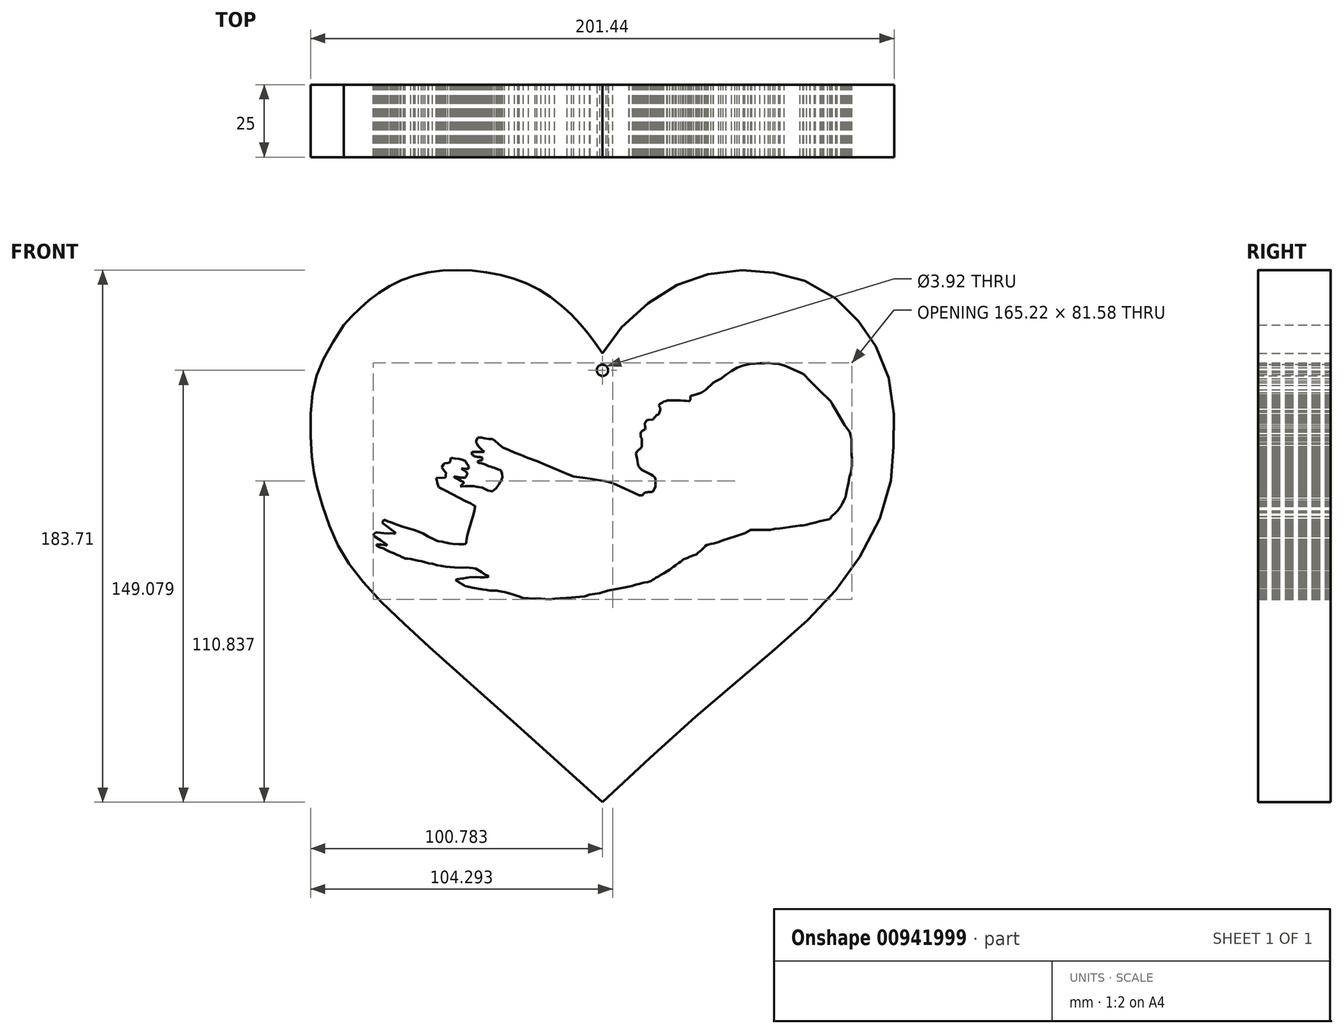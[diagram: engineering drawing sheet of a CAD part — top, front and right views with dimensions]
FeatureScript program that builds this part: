
annotation { "Feature Type Name" : "Feature", "Feature Type Description" : "" }
export const myFeature = defineFeature(function(context is Context, id is Id, definition is map)
    precondition{}
    {
        {
            var Q0;
            Q0=qCreatedBy(makeId("Front.planeOp"),FACE);
            var sketch = newSketch(context, id + "F0", { "sketchPlane" : qUnion([Q0])});
            skFitSpline(sketch, "E0", {"points": [v(-91.87, 46.62) * mm, v(-81.76, 56.16) * mm, v(-66.44, 63.96) * mm, v(-45.34, 65.12) * mm, v(-26.55, 59.92) * mm, v(-12.1, 48.93) * mm, v(-2.52, 36.86) * mm], "startDerivative": vector(63.3, 66.27) * mm, "endDerivative": vector(56.32, -78.36) * mm});
            skFitSpline(sketch, "E1", {"points": [v(-2.52, 36.86) * mm, v(5.39, 47.35) * mm, v(17.93, 57.31) * mm, v(29.62, 62.99) * mm, v(43.71, 65.4) * mm, v(56.26, 64.7) * mm, v(68.97, 61.1) * mm, v(81.7, 52.5) * mm, v(88.9, 43.74) * mm, v(95.1, 32.22) * mm, v(98.02, 16.24) * mm, v(97.85, 3) * mm, v(95.96, -12.11) * mm, v(86.85, -32.57) * mm, v(74.47, -49.06) * mm, v(57.8, -64.7) * mm, v(33.23, -85.5) * mm, v(-2.52, -118.15) * mm], "startDerivative": vector(138.08, 210.1) * mm, "endDerivative": vector(-379.46, -353.8) * mm});
            skFitSpline(sketch, "E2", {"points": [v(-2.52, -118.15) * mm, v(-50.8, -74.84) * mm, v(-83.63, -43.9) * mm, v(-95.32, -26.38) * mm, v(-100.82, -10.05) * mm, v(-102.7, 0) * mm, v(-103.05, 18.82) * mm, v(-99.79, 32.74) * mm, v(-91.87, 46.62) * mm], "startDerivative": vector(-238.07, 214.29) * mm, "endDerivative": vector(86.52, 135.51) * mm});
            skSolve(sketch);
        }
        {
            var Q0;
            Q0 = qSketchRegion(id + "F0", true);
            extrude(context, id + "F1", {"entities" : qUnion([Q0]), "depth" : 25 * mm, "offsetDistance" : 25 * mm});
        }
        {
            var Q0;
            Q0=qCreatedBy(makeId("Front.planeOp"),FACE);
            var sketch = newSketch(context, id + "F2", { "sketchPlane" : qUnion([Q0])});
            skLineSegment(sketch, "E3", {"start": v(-47.5, 2.74) * mm, "end": v(-43.27, 2.74) * mm});
            skLineSegment(sketch, "E4", {"start": v(-43.27, 2.74) * mm, "end": v(-44.61, 3.9) * mm});
            skLineSegment(sketch, "E5", {"start": v(-44.61, 3.9) * mm, "end": v(-45.36, 4.67) * mm});
            skLineSegment(sketch, "E6", {"start": v(-45.36, 4.67) * mm, "end": v(-45.88, 5.5) * mm});
            skLineSegment(sketch, "E7", {"start": v(-45.88, 5.5) * mm, "end": v(-46.11, 6) * mm});
            skLineSegment(sketch, "E8", {"start": v(-46.11, 6) * mm, "end": v(-46.11, 6.37) * mm});
            skLineSegment(sketch, "E9", {"start": v(-46.11, 6.37) * mm, "end": v(-46.11, 6.55) * mm});
            skLineSegment(sketch, "E10", {"start": v(-46.11, 6.55) * mm, "end": v(-45.84, 7.16) * mm});
            skLineSegment(sketch, "E11", {"start": v(-45.84, 7.16) * mm, "end": v(-45.54, 7.7) * mm});
            skLineSegment(sketch, "E12", {"start": v(-45.54, 7.7) * mm, "end": v(-45.2, 7.7) * mm});
            skLineSegment(sketch, "E13", {"start": v(-45.2, 7.7) * mm, "end": v(-44.32, 7.7) * mm});
            skLineSegment(sketch, "E14", {"start": v(-44.32, 7.7) * mm, "end": v(-43.25, 7.5) * mm});
            skLineSegment(sketch, "E15", {"start": v(-43.25, 7.5) * mm, "end": v(-41.85, 7.28) * mm});
            skLineSegment(sketch, "E16", {"start": v(-41.85, 7.28) * mm, "end": v(-40.8, 7.28) * mm});
            skLineSegment(sketch, "E17", {"start": v(-40.8, 7.28) * mm, "end": v(-40.46, 7.28) * mm});
            skLineSegment(sketch, "E18", {"start": v(-40.46, 7.28) * mm, "end": v(-39.65, 6.55) * mm});
            skLineSegment(sketch, "E19", {"start": v(-39.65, 6.55) * mm, "end": v(-38.36, 5.41) * mm});
            skLineSegment(sketch, "E20", {"start": v(-38.36, 5.41) * mm, "end": v(-37.02, 4.35) * mm});
            skLineSegment(sketch, "E21", {"start": v(-37.02, 4.35) * mm, "end": v(-34.84, 3.4) * mm});
            skLineSegment(sketch, "E22", {"start": v(-34.84, 3.4) * mm, "end": v(-32.85, 2.55) * mm});
            skLineSegment(sketch, "E23", {"start": v(-32.85, 2.55) * mm, "end": v(-30.76, 1.72) * mm});
            skLineSegment(sketch, "E24", {"start": v(-30.76, 1.72) * mm, "end": v(-28.4, 0.79) * mm});
            skLineSegment(sketch, "E25", {"start": v(-28.4, 0.79) * mm, "end": v(-25.18, -0.46) * mm});
            skLineSegment(sketch, "E26", {"start": v(-25.18, -0.46) * mm, "end": v(-22.25, -1.73) * mm});
            skLineSegment(sketch, "E27", {"start": v(-22.25, -1.73) * mm, "end": v(-18.33, -3.37) * mm});
            skLineSegment(sketch, "E28", {"start": v(-18.33, -3.37) * mm, "end": v(-14.77, -4.82) * mm});
            skLineSegment(sketch, "E29", {"start": v(-14.77, -4.82) * mm, "end": v(-12.5, -5.8) * mm});
            skLineSegment(sketch, "E30", {"start": v(-12.5, -5.8) * mm, "end": v(-9.4, -6.15) * mm});
            skLineSegment(sketch, "E31", {"start": v(-9.4, -6.15) * mm, "end": v(-6.74, -6.47) * mm});
            skLineSegment(sketch, "E32", {"start": v(-6.74, -6.47) * mm, "end": v(-3.68, -7.02) * mm});
            skLineSegment(sketch, "E33", {"start": v(-3.68, -7.02) * mm, "end": v(-1.27, -7.45) * mm});
            skLineSegment(sketch, "E34", {"start": v(-1.27, -7.45) * mm, "end": v(0.97, -8.08) * mm});
            skLineSegment(sketch, "E35", {"start": v(0.97, -8.08) * mm, "end": v(2.95, -8.93) * mm});
            skLineSegment(sketch, "E36", {"start": v(2.95, -8.93) * mm, "end": v(5.15, -9.88) * mm});
            skLineSegment(sketch, "E37", {"start": v(5.15, -9.88) * mm, "end": v(6.66, -10.53) * mm});
            skLineSegment(sketch, "E38", {"start": v(6.66, -10.53) * mm, "end": v(8.24, -11.37) * mm});
            skLineSegment(sketch, "E39", {"start": v(8.24, -11.37) * mm, "end": v(9.38, -11.86) * mm});
            skLineSegment(sketch, "E40", {"start": v(9.38, -11.86) * mm, "end": v(10.1, -12.17) * mm});
            skLineSegment(sketch, "E41", {"start": v(10.1, -12.17) * mm, "end": v(10.85, -12.17) * mm});
            skLineSegment(sketch, "E42", {"start": v(10.85, -12.17) * mm, "end": v(11.25, -12.17) * mm});
            skLineSegment(sketch, "E43", {"start": v(11.25, -12.17) * mm, "end": v(11.52, -11.84) * mm});
            skLineSegment(sketch, "E44", {"start": v(11.52, -11.84) * mm, "end": v(11.78, -11.63) * mm});
            skLineSegment(sketch, "E45", {"start": v(11.78, -11.63) * mm, "end": v(12.21, -11.25) * mm});
            skLineSegment(sketch, "E46", {"start": v(12.21, -11.25) * mm, "end": v(12.35, -11.25) * mm});
            skLineSegment(sketch, "E47", {"start": v(12.35, -11.25) * mm, "end": v(12.8, -11.19) * mm});
            skLineSegment(sketch, "E48", {"start": v(12.8, -11.19) * mm, "end": v(13.3, -11.12) * mm});
            skLineSegment(sketch, "E49", {"start": v(13.3, -11.12) * mm, "end": v(13.95, -11.12) * mm});
            skLineSegment(sketch, "E50", {"start": v(13.95, -11.12) * mm, "end": v(14.61, -11.08) * mm});
            skLineSegment(sketch, "E51", {"start": v(14.61, -11.08) * mm, "end": v(15, -10.85) * mm});
            skLineSegment(sketch, "E52", {"start": v(15, -10.85) * mm, "end": v(15.18, -10.41) * mm});
            skLineSegment(sketch, "E53", {"start": v(15.18, -10.41) * mm, "end": v(15.4, -9.88) * mm});
            skLineSegment(sketch, "E54", {"start": v(15.4, -9.88) * mm, "end": v(15.7, -9.2) * mm});
            skLineSegment(sketch, "E55", {"start": v(15.7, -9.2) * mm, "end": v(15.7, -7.4) * mm});
            skLineSegment(sketch, "E56", {"start": v(15.7, -7.4) * mm, "end": v(15.7, -6.76) * mm});
            skLineSegment(sketch, "E57", {"start": v(15.7, -6.76) * mm, "end": v(15.6, -6.08) * mm});
            skLineSegment(sketch, "E58", {"start": v(15.6, -6.08) * mm, "end": v(14.76, -5.4) * mm});
            skLineSegment(sketch, "E59", {"start": v(14.76, -5.4) * mm, "end": v(14.08, -4.98) * mm});
            skLineSegment(sketch, "E60", {"start": v(14.08, -4.98) * mm, "end": v(11.04, -3.46) * mm});
            skLineSegment(sketch, "E61", {"start": v(11.04, -3.46) * mm, "end": v(10.3, -2.72) * mm});
            skLineSegment(sketch, "E62", {"start": v(10.3, -2.72) * mm, "end": v(9.79, -1.95) * mm});
            skLineSegment(sketch, "E63", {"start": v(9.79, -1.95) * mm, "end": v(9.58, -0.4) * mm});
            skLineSegment(sketch, "E64", {"start": v(9.58, -0.4) * mm, "end": v(9.44, 0.6) * mm});
            skLineSegment(sketch, "E65", {"start": v(9.44, 0.6) * mm, "end": v(9.16, 1.53) * mm});
            skLineSegment(sketch, "E66", {"start": v(9.16, 1.53) * mm, "end": v(9.07, 2.19) * mm});
            skLineSegment(sketch, "E67", {"start": v(9.07, 2.19) * mm, "end": v(9.3, 2.72) * mm});
            skLineSegment(sketch, "E68", {"start": v(9.3, 2.72) * mm, "end": v(9.79, 3.34) * mm});
            skLineSegment(sketch, "E69", {"start": v(9.79, 3.34) * mm, "end": v(10.83, 4.16) * mm});
            skLineSegment(sketch, "E70", {"start": v(10.83, 4.16) * mm, "end": v(11.06, 4.7) * mm});
            skLineSegment(sketch, "E71", {"start": v(11.06, 4.7) * mm, "end": v(11.06, 7.11) * mm});
            skLineSegment(sketch, "E72", {"start": v(11.06, 7.11) * mm, "end": v(11.02, 7.43) * mm});
            skLineSegment(sketch, "E73", {"start": v(11.02, 7.43) * mm, "end": v(10.67, 7.85) * mm});
            skLineSegment(sketch, "E74", {"start": v(10.67, 7.85) * mm, "end": v(10.63, 8.54) * mm});
            skLineSegment(sketch, "E75", {"start": v(10.63, 8.54) * mm, "end": v(10.53, 8.8) * mm});
            skLineSegment(sketch, "E76", {"start": v(10.53, 8.8) * mm, "end": v(10.77, 9.68) * mm});
            skLineSegment(sketch, "E77", {"start": v(10.77, 9.68) * mm, "end": v(11.35, 10.08) * mm});
            skLineSegment(sketch, "E78", {"start": v(11.35, 10.08) * mm, "end": v(11.63, 10.21) * mm});
            skLineSegment(sketch, "E79", {"start": v(11.63, 10.21) * mm, "end": v(11.87, 10.37) * mm});
            skLineSegment(sketch, "E80", {"start": v(11.87, 10.37) * mm, "end": v(12.21, 10.55) * mm});
            skLineSegment(sketch, "E81", {"start": v(12.21, 10.55) * mm, "end": v(12.3, 10.74) * mm});
            skLineSegment(sketch, "E82", {"start": v(12.3, 10.74) * mm, "end": v(12.25, 11.45) * mm});
            skPoint(sketch, "E82.endSnap0", {"position": v(12.25, 10.65) * mm});
            skLineSegment(sketch, "E83", {"start": v(12.25, 11.45) * mm, "end": v(12.13, 12.34) * mm});
            skLineSegment(sketch, "E84", {"start": v(12.13, 12.34) * mm, "end": v(12.1, 12.64) * mm});
            skLineSegment(sketch, "E85", {"start": v(12.1, 12.64) * mm, "end": v(12.3, 12.97) * mm});
            skLineSegment(sketch, "E86", {"start": v(12.3, 12.97) * mm, "end": v(12.54, 13.41) * mm});
            skLineSegment(sketch, "E87", {"start": v(12.54, 13.41) * mm, "end": v(12.73, 13.73) * mm});
            skLineSegment(sketch, "E88", {"start": v(12.73, 13.73) * mm, "end": v(13.3, 13.8) * mm});
            skLineSegment(sketch, "E89", {"start": v(13.3, 13.8) * mm, "end": v(14.96, 13.96) * mm});
            skLineSegment(sketch, "E90", {"start": v(14.96, 13.96) * mm, "end": v(15.3, 14.43) * mm});
            skLineSegment(sketch, "E91", {"start": v(15.3, 14.43) * mm, "end": v(15.76, 15.03) * mm});
            skLineSegment(sketch, "E92", {"start": v(15.76, 15.03) * mm, "end": v(16.15, 15.46) * mm});
            skLineSegment(sketch, "E93", {"start": v(16.15, 15.46) * mm, "end": v(16.55, 15.66) * mm});
            skLineSegment(sketch, "E94", {"start": v(16.55, 15.66) * mm, "end": v(16.88, 15.7) * mm});
            skLineSegment(sketch, "E95", {"start": v(16.88, 15.7) * mm, "end": v(17.2, 16.44) * mm});
            skLineSegment(sketch, "E96", {"start": v(17.2, 16.44) * mm, "end": v(17.4, 17.14) * mm});
            skLineSegment(sketch, "E97", {"start": v(17.4, 17.14) * mm, "end": v(17.4, 17.7) * mm});
            skLineSegment(sketch, "E98", {"start": v(17.4, 17.7) * mm, "end": v(17.4, 17.97) * mm});
            skLineSegment(sketch, "E99", {"start": v(17.4, 17.97) * mm, "end": v(17.19, 18.4) * mm});
            skLineSegment(sketch, "E100", {"start": v(17.19, 18.4) * mm, "end": v(16.94, 18.75) * mm});
            skLineSegment(sketch, "E101", {"start": v(16.94, 18.75) * mm, "end": v(17.02, 19) * mm});
            skLineSegment(sketch, "E102", {"start": v(17.02, 19) * mm, "end": v(17.4, 19.35) * mm});
            skLineSegment(sketch, "E103", {"start": v(17.4, 19.35) * mm, "end": v(18.2, 19.82) * mm});
            skLineSegment(sketch, "E104", {"start": v(18.2, 19.82) * mm, "end": v(18.59, 20.18) * mm});
            skLineSegment(sketch, "E105", {"start": v(18.59, 20.18) * mm, "end": v(19.28, 20.35) * mm});
            skLineSegment(sketch, "E106", {"start": v(19.28, 20.35) * mm, "end": v(19.94, 20.51) * mm});
            skLineSegment(sketch, "E107", {"start": v(19.94, 20.51) * mm, "end": v(21.56, 20.6) * mm});
            skLineSegment(sketch, "E108", {"start": v(21.56, 20.6) * mm, "end": v(22.93, 20.6) * mm});
            skLineSegment(sketch, "E109", {"start": v(22.93, 20.6) * mm, "end": v(24.37, 20.6) * mm});
            skLineSegment(sketch, "E110", {"start": v(24.37, 20.6) * mm, "end": v(25.5, 20.49) * mm});
            skLineSegment(sketch, "E111", {"start": v(25.5, 20.49) * mm, "end": v(26.3, 20.4) * mm});
            skLineSegment(sketch, "E112", {"start": v(26.3, 20.4) * mm, "end": v(27.3, 20.33) * mm});
            skLineSegment(sketch, "E113", {"start": v(27.3, 20.33) * mm, "end": v(27.61, 20.37) * mm});
            skLineSegment(sketch, "E114", {"start": v(27.61, 20.37) * mm, "end": v(27.75, 20.83) * mm});
            skLineSegment(sketch, "E115", {"start": v(27.75, 20.83) * mm, "end": v(27.86, 21.46) * mm});
            skLineSegment(sketch, "E116", {"start": v(27.86, 21.46) * mm, "end": v(27.86, 21.9) * mm});
            skLineSegment(sketch, "E117", {"start": v(27.86, 21.9) * mm, "end": v(28.05, 22.17) * mm});
            skLineSegment(sketch, "E118", {"start": v(28.05, 22.17) * mm, "end": v(28.38, 22.22) * mm});
            skLineSegment(sketch, "E119", {"start": v(28.38, 22.22) * mm, "end": v(29.73, 22.55) * mm});
            skLineSegment(sketch, "E120", {"start": v(29.73, 22.55) * mm, "end": v(31.6, 23.26) * mm});
            skLineSegment(sketch, "E121", {"start": v(31.6, 23.26) * mm, "end": v(33.1, 24.27) * mm});
            skLineSegment(sketch, "E122", {"start": v(33.1, 24.27) * mm, "end": v(34.17, 25.3) * mm});
            skLineSegment(sketch, "E123", {"start": v(34.17, 25.3) * mm, "end": v(34.87, 25.96) * mm});
            skLineSegment(sketch, "E124", {"start": v(34.87, 25.96) * mm, "end": v(35.62, 26.67) * mm});
            skLineSegment(sketch, "E125", {"start": v(35.62, 26.67) * mm, "end": v(36.62, 27.17) * mm});
            skLineSegment(sketch, "E126", {"start": v(36.62, 27.17) * mm, "end": v(38.33, 28) * mm});
            skLineSegment(sketch, "E127", {"start": v(38.33, 28) * mm, "end": v(40.14, 29.43) * mm});
            skLineSegment(sketch, "E128", {"start": v(40.14, 29.43) * mm, "end": v(42.03, 30.7) * mm});
            skLineSegment(sketch, "E129", {"start": v(42.03, 30.7) * mm, "end": v(43.95, 31.81) * mm});
            skLineSegment(sketch, "E130", {"start": v(43.95, 31.81) * mm, "end": v(46.1, 32.63) * mm});
            skLineSegment(sketch, "E131", {"start": v(46.1, 32.63) * mm, "end": v(47.79, 33.04) * mm});
            skLineSegment(sketch, "E132", {"start": v(47.79, 33.04) * mm, "end": v(48.97, 33.2) * mm});
            skLineSegment(sketch, "E133", {"start": v(48.97, 33.2) * mm, "end": v(50.22, 33.32) * mm});
            skLineSegment(sketch, "E134", {"start": v(50.22, 33.32) * mm, "end": v(51.83, 33.4) * mm});
            skLineSegment(sketch, "E135", {"start": v(51.83, 33.4) * mm, "end": v(53.49, 33.4) * mm});
            skLineSegment(sketch, "E136", {"start": v(53.49, 33.4) * mm, "end": v(54.73, 33.48) * mm});
            skLineSegment(sketch, "E137", {"start": v(54.73, 33.48) * mm, "end": v(56.4, 33.32) * mm});
            skLineSegment(sketch, "E138", {"start": v(56.4, 33.32) * mm, "end": v(58.33, 33.1) * mm});
            skLineSegment(sketch, "E139", {"start": v(58.33, 33.1) * mm, "end": v(60.14, 32.56) * mm});
            skLineSegment(sketch, "E140", {"start": v(60.14, 32.56) * mm, "end": v(61.58, 31.94) * mm});
            skLineSegment(sketch, "E141", {"start": v(61.58, 31.94) * mm, "end": v(63.42, 31.15) * mm});
            skLineSegment(sketch, "E142", {"start": v(63.42, 31.15) * mm, "end": v(65.68, 30.18) * mm});
            skLineSegment(sketch, "E143", {"start": v(65.68, 30.18) * mm, "end": v(66.92, 29.5) * mm});
            skLineSegment(sketch, "E144", {"start": v(66.92, 29.5) * mm, "end": v(69.13, 27.34) * mm});
            skLineSegment(sketch, "E145", {"start": v(69.13, 27.34) * mm, "end": v(70.65, 25.73) * mm});
            skLineSegment(sketch, "E146", {"start": v(70.65, 25.73) * mm, "end": v(73.16, 23.23) * mm});
            skLineSegment(sketch, "E147", {"start": v(73.16, 23.23) * mm, "end": v(75.14, 21.34) * mm});
            skLineSegment(sketch, "E148", {"start": v(75.14, 21.34) * mm, "end": v(76.28, 20.14) * mm});
            skLineSegment(sketch, "E149", {"start": v(76.28, 20.14) * mm, "end": v(76.87, 19.2) * mm});
            skLineSegment(sketch, "E150", {"start": v(76.87, 19.2) * mm, "end": v(78.4, 16.66) * mm});
            skLineSegment(sketch, "E151", {"start": v(78.4, 16.66) * mm, "end": v(79.82, 14.22) * mm});
            skLineSegment(sketch, "E152", {"start": v(79.82, 14.22) * mm, "end": v(81, 12.1) * mm});
            skLineSegment(sketch, "E153", {"start": v(81, 12.1) * mm, "end": v(82.78, 9.6) * mm});
            skLineSegment(sketch, "E154", {"start": v(82.78, 9.6) * mm, "end": v(83.1, 8.73) * mm});
            skLineSegment(sketch, "E155", {"start": v(83.1, 8.73) * mm, "end": v(83.49, 7.11) * mm});
            skLineSegment(sketch, "E156", {"start": v(83.49, 7.11) * mm, "end": v(83.49, 4.84) * mm});
            skLineSegment(sketch, "E157", {"start": v(83.49, 4.84) * mm, "end": v(83.49, 2.17) * mm});
            skLineSegment(sketch, "E158", {"start": v(83.49, 2.17) * mm, "end": v(83.6, 0.2) * mm});
            skLineSegment(sketch, "E159", {"start": v(83.6, 0.2) * mm, "end": v(83.6, -1.95) * mm});
            skLineSegment(sketch, "E160", {"start": v(83.6, -1.95) * mm, "end": v(83.46, -2.93) * mm});
            skLineSegment(sketch, "E161", {"start": v(83.46, -2.93) * mm, "end": v(83.22, -4.44) * mm});
            skLineSegment(sketch, "E162", {"start": v(83.22, -4.44) * mm, "end": v(82.93, -5.4) * mm});
            skLineSegment(sketch, "E163", {"start": v(82.93, -5.4) * mm, "end": v(82.74, -6.05) * mm});
            skLineSegment(sketch, "E164", {"start": v(82.74, -6.05) * mm, "end": v(82.41, -7.75) * mm});
            skLineSegment(sketch, "E165", {"start": v(82.41, -7.75) * mm, "end": v(82.22, -8.93) * mm});
            skLineSegment(sketch, "E166", {"start": v(82.22, -8.93) * mm, "end": v(81.9, -9.98) * mm});
            skLineSegment(sketch, "E167", {"start": v(81.9, -9.98) * mm, "end": v(81.54, -11.88) * mm});
            skLineSegment(sketch, "E168", {"start": v(81.54, -11.88) * mm, "end": v(81.42, -12.68) * mm});
            skLineSegment(sketch, "E169", {"start": v(81.42, -12.68) * mm, "end": v(81.07, -13.49) * mm});
            skLineSegment(sketch, "E170", {"start": v(81.07, -13.49) * mm, "end": v(80.78, -14.07) * mm});
            skLineSegment(sketch, "E171", {"start": v(80.78, -14.07) * mm, "end": v(80.41, -14.7) * mm});
            skLineSegment(sketch, "E172", {"start": v(80.41, -14.7) * mm, "end": v(80.14, -15.21) * mm});
            skLineSegment(sketch, "E173", {"start": v(80.14, -15.21) * mm, "end": v(79.77, -16.08) * mm});
            skLineSegment(sketch, "E174", {"start": v(79.77, -16.08) * mm, "end": v(78.51, -17.63) * mm});
            skLineSegment(sketch, "E175", {"start": v(78.51, -17.63) * mm, "end": v(77.97, -18.14) * mm});
            skLineSegment(sketch, "E176", {"start": v(77.97, -18.14) * mm, "end": v(77.2, -18.92) * mm});
            skLineSegment(sketch, "E177", {"start": v(77.2, -18.92) * mm, "end": v(76.5, -19.62) * mm});
            skLineSegment(sketch, "E178", {"start": v(76.5, -19.62) * mm, "end": v(76.16, -20.13) * mm});
            skLineSegment(sketch, "E179", {"start": v(76.16, -20.13) * mm, "end": v(75.93, -20.46) * mm});
            skLineSegment(sketch, "E180", {"start": v(75.93, -20.46) * mm, "end": v(75.16, -20.64) * mm});
            skLineSegment(sketch, "E181", {"start": v(75.16, -20.64) * mm, "end": v(73.97, -20.8) * mm});
            skLineSegment(sketch, "E182", {"start": v(73.97, -20.8) * mm, "end": v(73.4, -21.02) * mm});
            skLineSegment(sketch, "E183", {"start": v(73.4, -21.02) * mm, "end": v(72.61, -21.12) * mm});
            skLineSegment(sketch, "E184", {"start": v(72.61, -21.12) * mm, "end": v(70.97, -21.6) * mm});
            skLineSegment(sketch, "E185", {"start": v(70.97, -21.6) * mm, "end": v(69.25, -21.96) * mm});
            skLineSegment(sketch, "E186", {"start": v(69.25, -21.96) * mm, "end": v(67.97, -22.33) * mm});
            skLineSegment(sketch, "E187", {"start": v(67.97, -22.33) * mm, "end": v(66.72, -22.58) * mm});
            skLineSegment(sketch, "E188", {"start": v(66.72, -22.58) * mm, "end": v(65.64, -22.65) * mm});
            skLineSegment(sketch, "E189", {"start": v(65.64, -22.65) * mm, "end": v(64.03, -22.86) * mm});
            skLineSegment(sketch, "E190", {"start": v(64.03, -22.86) * mm, "end": v(62.55, -23.07) * mm});
            skLineSegment(sketch, "E191", {"start": v(62.55, -23.07) * mm, "end": v(60.79, -23.3) * mm});
            skLineSegment(sketch, "E192", {"start": v(60.79, -23.3) * mm, "end": v(58.74, -23.58) * mm});
            skLineSegment(sketch, "E193", {"start": v(58.74, -23.58) * mm, "end": v(56.96, -23.74) * mm});
            skLineSegment(sketch, "E194", {"start": v(56.96, -23.74) * mm, "end": v(55.38, -24.2) * mm});
            skLineSegment(sketch, "E195", {"start": v(55.38, -24.2) * mm, "end": v(51.48, -24.2) * mm});
            skLineSegment(sketch, "E196", {"start": v(51.48, -24.2) * mm, "end": v(48.66, -24.2) * mm});
            skLineSegment(sketch, "E197", {"start": v(48.66, -24.2) * mm, "end": v(46.55, -25.27) * mm});
            skLineSegment(sketch, "E198", {"start": v(46.55, -25.27) * mm, "end": v(44.7, -25.97) * mm});
            skLineSegment(sketch, "E199", {"start": v(44.7, -25.97) * mm, "end": v(43.12, -26.44) * mm});
            skLineSegment(sketch, "E200", {"start": v(43.12, -26.44) * mm, "end": v(39.07, -27.73) * mm});
            skLineSegment(sketch, "E201", {"start": v(39.07, -27.73) * mm, "end": v(37.6, -28.28) * mm});
            skLineSegment(sketch, "E202", {"start": v(37.6, -28.28) * mm, "end": v(36.66, -28.56) * mm});
            skLineSegment(sketch, "E203", {"start": v(36.66, -28.56) * mm, "end": v(35.83, -28.8) * mm});
            skLineSegment(sketch, "E204", {"start": v(35.83, -28.8) * mm, "end": v(34.93, -28.99) * mm});
            skLineSegment(sketch, "E205", {"start": v(34.93, -28.99) * mm, "end": v(34.06, -29.24) * mm});
            skLineSegment(sketch, "E206", {"start": v(34.06, -29.24) * mm, "end": v(33.56, -29.38) * mm});
            skLineSegment(sketch, "E207", {"start": v(33.56, -29.38) * mm, "end": v(32.88, -29.78) * mm});
            skLineSegment(sketch, "E208", {"start": v(32.88, -29.78) * mm, "end": v(32.68, -30.15) * mm});
            skLineSegment(sketch, "E209", {"start": v(32.68, -30.15) * mm, "end": v(31.9, -30.94) * mm});
            skLineSegment(sketch, "E210", {"start": v(31.9, -30.94) * mm, "end": v(31.66, -31.1) * mm});
            skLineSegment(sketch, "E211", {"start": v(31.66, -31.1) * mm, "end": v(30.94, -31.65) * mm});
            skLineSegment(sketch, "E212", {"start": v(30.94, -31.65) * mm, "end": v(30.54, -32.05) * mm});
            skLineSegment(sketch, "E213", {"start": v(30.54, -32.05) * mm, "end": v(30.07, -32.46) * mm});
            skLineSegment(sketch, "E214", {"start": v(30.07, -32.46) * mm, "end": v(29.81, -32.68) * mm});
            skLineSegment(sketch, "E215", {"start": v(29.81, -32.68) * mm, "end": v(28.92, -32.97) * mm});
            skLineSegment(sketch, "E216", {"start": v(28.92, -32.97) * mm, "end": v(27.92, -33.35) * mm});
            skLineSegment(sketch, "E217", {"start": v(27.92, -33.35) * mm, "end": v(27.37, -33.57) * mm});
            skLineSegment(sketch, "E218", {"start": v(27.37, -33.57) * mm, "end": v(26.93, -33.82) * mm});
            skLineSegment(sketch, "E219", {"start": v(26.93, -33.82) * mm, "end": v(26.18, -34.04) * mm});
            skLineSegment(sketch, "E220", {"start": v(26.18, -34.04) * mm, "end": v(25.39, -34.34) * mm});
            skLineSegment(sketch, "E221", {"start": v(25.39, -34.34) * mm, "end": v(25, -34.65) * mm});
            skLineSegment(sketch, "E222", {"start": v(25, -34.65) * mm, "end": v(24.37, -35.2) * mm});
            skLineSegment(sketch, "E223", {"start": v(24.37, -35.2) * mm, "end": v(23.7, -35.6) * mm});
            skLineSegment(sketch, "E224", {"start": v(23.7, -35.6) * mm, "end": v(22.93, -36.14) * mm});
            skLineSegment(sketch, "E225", {"start": v(22.93, -36.14) * mm, "end": v(22.6, -36.45) * mm});
            skLineSegment(sketch, "E226", {"start": v(22.6, -36.45) * mm, "end": v(21.98, -36.91) * mm});
            skLineSegment(sketch, "E227", {"start": v(21.98, -36.91) * mm, "end": v(21.37, -37.39) * mm});
            skLineSegment(sketch, "E228", {"start": v(21.37, -37.39) * mm, "end": v(20.73, -37.9) * mm});
            skLineSegment(sketch, "E229", {"start": v(20.73, -37.9) * mm, "end": v(19.69, -38.53) * mm});
            skLineSegment(sketch, "E230", {"start": v(19.69, -38.53) * mm, "end": v(18.72, -39.1) * mm});
            skLineSegment(sketch, "E231", {"start": v(18.72, -39.1) * mm, "end": v(17.65, -39.7) * mm});
            skLineSegment(sketch, "E232", {"start": v(17.65, -39.7) * mm, "end": v(16.76, -40.26) * mm});
            skLineSegment(sketch, "E233", {"start": v(16.76, -40.26) * mm, "end": v(15.93, -40.72) * mm});
            skLineSegment(sketch, "E234", {"start": v(15.93, -40.72) * mm, "end": v(15.18, -41.13) * mm});
            skLineSegment(sketch, "E235", {"start": v(15.18, -41.13) * mm, "end": v(14.67, -41.46) * mm});
            skLineSegment(sketch, "E236", {"start": v(14.67, -41.46) * mm, "end": v(14.17, -41.76) * mm});
            skLineSegment(sketch, "E237", {"start": v(14.17, -41.76) * mm, "end": v(13.07, -42.18) * mm});
            skLineSegment(sketch, "E238", {"start": v(13.07, -42.18) * mm, "end": v(11.98, -42.37) * mm});
            skLineSegment(sketch, "E239", {"start": v(11.98, -42.37) * mm, "end": v(10.97, -42.57) * mm});
            skLineSegment(sketch, "E240", {"start": v(10.97, -42.57) * mm, "end": v(10.15, -42.77) * mm});
            skLineSegment(sketch, "E241", {"start": v(10.15, -42.77) * mm, "end": v(9.46, -42.98) * mm});
            skLineSegment(sketch, "E242", {"start": v(9.46, -42.98) * mm, "end": v(8.48, -43.2) * mm});
            skLineSegment(sketch, "E243", {"start": v(8.48, -43.2) * mm, "end": v(7.88, -43.43) * mm});
            skLineSegment(sketch, "E244", {"start": v(7.88, -43.43) * mm, "end": v(6.76, -43.67) * mm});
            skLineSegment(sketch, "E245", {"start": v(6.76, -43.67) * mm, "end": v(5.45, -43.91) * mm});
            skLineSegment(sketch, "E246", {"start": v(5.45, -43.91) * mm, "end": v(-0.58, -45.12) * mm});
            skLineSegment(sketch, "E247", {"start": v(-0.58, -45.12) * mm, "end": v(-3.49, -46) * mm});
            skLineSegment(sketch, "E248", {"start": v(-3.49, -46) * mm, "end": v(-6.97, -46.46) * mm});
            skLineSegment(sketch, "E249", {"start": v(-6.97, -46.46) * mm, "end": v(-8.83, -47.17) * mm});
            skLineSegment(sketch, "E250", {"start": v(-8.83, -47.17) * mm, "end": v(-10.42, -47.2) * mm});
            skLineSegment(sketch, "E251", {"start": v(-10.42, -47.2) * mm, "end": v(-13.16, -47.58) * mm});
            skLineSegment(sketch, "E252", {"start": v(-13.16, -47.58) * mm, "end": v(-16.48, -47.76) * mm});
            skLineSegment(sketch, "E253", {"start": v(-16.48, -47.76) * mm, "end": v(-19.08, -47.9) * mm});
            skLineSegment(sketch, "E254", {"start": v(-19.08, -47.9) * mm, "end": v(-20.77, -48.1) * mm});
            skLineSegment(sketch, "E255", {"start": v(-20.77, -48.1) * mm, "end": v(-23.75, -47.9) * mm});
            skLineSegment(sketch, "E256", {"start": v(-23.75, -47.9) * mm, "end": v(-25.76, -47.95) * mm});
            skLineSegment(sketch, "E257", {"start": v(-25.76, -47.95) * mm, "end": v(-28.12, -47.79) * mm});
            skLineSegment(sketch, "E258", {"start": v(-28.12, -47.79) * mm, "end": v(-29.88, -47.79) * mm});
            skLineSegment(sketch, "E259", {"start": v(-29.88, -47.79) * mm, "end": v(-31.2, -47.17) * mm});
            skLineSegment(sketch, "E260", {"start": v(-31.2, -47.17) * mm, "end": v(-31.72, -46.96) * mm});
            skLineSegment(sketch, "E261", {"start": v(-31.72, -46.96) * mm, "end": v(-33.27, -46.5) * mm});
            skLineSegment(sketch, "E262", {"start": v(-33.27, -46.5) * mm, "end": v(-34.88, -46) * mm});
            skLineSegment(sketch, "E263", {"start": v(-34.88, -46) * mm, "end": v(-36.25, -45.58) * mm});
            skLineSegment(sketch, "E264", {"start": v(-36.25, -45.58) * mm, "end": v(-37.26, -45.43) * mm});
            skLineSegment(sketch, "E265", {"start": v(-37.26, -45.43) * mm, "end": v(-39.15, -45.13) * mm});
            skLineSegment(sketch, "E266", {"start": v(-39.15, -45.13) * mm, "end": v(-41.4, -45.08) * mm});
            skLineSegment(sketch, "E267", {"start": v(-41.4, -45.08) * mm, "end": v(-42.65, -44.8) * mm});
            skLineSegment(sketch, "E268", {"start": v(-42.65, -44.8) * mm, "end": v(-43.79, -44.7) * mm});
            skLineSegment(sketch, "E269", {"start": v(-43.79, -44.7) * mm, "end": v(-45.81, -44.38) * mm});
            skLineSegment(sketch, "E270", {"start": v(-45.81, -44.38) * mm, "end": v(-47.47, -44.12) * mm});
            skLineSegment(sketch, "E271", {"start": v(-47.47, -44.12) * mm, "end": v(-49.2, -43.75) * mm});
            skLineSegment(sketch, "E272", {"start": v(-49.2, -43.75) * mm, "end": v(-49.95, -43.58) * mm});
            skLineSegment(sketch, "E273", {"start": v(-49.95, -43.58) * mm, "end": v(-50.39, -43.15) * mm});
            skLineSegment(sketch, "E274", {"start": v(-50.39, -43.15) * mm, "end": v(-50.87, -42.89) * mm});
            skLineSegment(sketch, "E275", {"start": v(-50.87, -42.89) * mm, "end": v(-51.38, -42.58) * mm});
            skLineSegment(sketch, "E276", {"start": v(-51.38, -42.58) * mm, "end": v(-51.7, -42.5) * mm});
            skLineSegment(sketch, "E277", {"start": v(-51.7, -42.5) * mm, "end": v(-52, -42.2) * mm});
            skLineSegment(sketch, "E278", {"start": v(-52, -42.2) * mm, "end": v(-52.3, -42.01) * mm});
            skLineSegment(sketch, "E279", {"start": v(-52.3, -42.01) * mm, "end": v(-52.62, -41.81) * mm});
            skLineSegment(sketch, "E280", {"start": v(-52.62, -41.81) * mm, "end": v(-53.16, -41.38) * mm});
            skLineSegment(sketch, "E281", {"start": v(-53.16, -41.38) * mm, "end": v(-52.78, -41.22) * mm});
            skLineSegment(sketch, "E282", {"start": v(-52.78, -41.22) * mm, "end": v(-51.86, -41.09) * mm});
            skLineSegment(sketch, "E283", {"start": v(-51.86, -41.09) * mm, "end": v(-50.64, -40.93) * mm});
            skLineSegment(sketch, "E284", {"start": v(-50.64, -40.93) * mm, "end": v(-49.33, -40.71) * mm});
            skLineSegment(sketch, "E285", {"start": v(-49.33, -40.71) * mm, "end": v(-48.56, -40.5) * mm});
            skLineSegment(sketch, "E286", {"start": v(-48.56, -40.5) * mm, "end": v(-46.21, -40.4) * mm});
            skLineSegment(sketch, "E287", {"start": v(-46.21, -40.4) * mm, "end": v(-44.87, -40.5) * mm});
            skLineSegment(sketch, "E288", {"start": v(-44.87, -40.5) * mm, "end": v(-43.3, -40.47) * mm});
            skLineSegment(sketch, "E289", {"start": v(-43.3, -40.47) * mm, "end": v(-42.41, -40.44) * mm});
            skLineSegment(sketch, "E290", {"start": v(-42.41, -40.44) * mm, "end": v(-41.98, -40.45) * mm});
            skLineSegment(sketch, "E291", {"start": v(-41.98, -40.45) * mm, "end": v(-41.86, -40.3) * mm});
            skLineSegment(sketch, "E292", {"start": v(-41.86, -40.3) * mm, "end": v(-41.85, -40.1) * mm});
            skLineSegment(sketch, "E293", {"start": v(-41.85, -40.1) * mm, "end": v(-43.24, -39.5) * mm});
            skLineSegment(sketch, "E294", {"start": v(-43.24, -39.5) * mm, "end": v(-44.24, -38.76) * mm});
            skLineSegment(sketch, "E295", {"start": v(-44.24, -38.76) * mm, "end": v(-45.2, -38.2) * mm});
            skLineSegment(sketch, "E296", {"start": v(-45.2, -38.2) * mm, "end": v(-46.42, -37.48) * mm});
            skLineSegment(sketch, "E297", {"start": v(-46.42, -37.48) * mm, "end": v(-47.22, -37.3) * mm});
            skLineSegment(sketch, "E298", {"start": v(-47.22, -37.3) * mm, "end": v(-49.48, -37.14) * mm});
            skLineSegment(sketch, "E299", {"start": v(-49.48, -37.14) * mm, "end": v(-51.18, -37.2) * mm});
            skLineSegment(sketch, "E300", {"start": v(-51.18, -37.2) * mm, "end": v(-53.62, -37.1) * mm});
            skLineSegment(sketch, "E301", {"start": v(-53.62, -37.1) * mm, "end": v(-55.17, -37.01) * mm});
            skLineSegment(sketch, "E302", {"start": v(-55.17, -37.01) * mm, "end": v(-56.65, -36.87) * mm});
            skLineSegment(sketch, "E303", {"start": v(-56.65, -36.87) * mm, "end": v(-58.1, -36.59) * mm});
            skLineSegment(sketch, "E304", {"start": v(-58.1, -36.59) * mm, "end": v(-59.69, -36.3) * mm});
            skLineSegment(sketch, "E305", {"start": v(-59.69, -36.3) * mm, "end": v(-61.15, -35.9) * mm});
            skLineSegment(sketch, "E306", {"start": v(-61.15, -35.9) * mm, "end": v(-62.48, -35.68) * mm});
            skLineSegment(sketch, "E307", {"start": v(-62.48, -35.68) * mm, "end": v(-63.76, -35.38) * mm});
            skLineSegment(sketch, "E308", {"start": v(-63.76, -35.38) * mm, "end": v(-64.97, -34.99) * mm});
            skLineSegment(sketch, "E309", {"start": v(-64.97, -34.99) * mm, "end": v(-66.02, -34.78) * mm});
            skLineSegment(sketch, "E310", {"start": v(-66.02, -34.78) * mm, "end": v(-67.75, -34.42) * mm});
            skLineSegment(sketch, "E311", {"start": v(-67.75, -34.42) * mm, "end": v(-68.7, -34.2) * mm});
            skLineSegment(sketch, "E312", {"start": v(-68.7, -34.2) * mm, "end": v(-69.82, -34.08) * mm});
            skLineSegment(sketch, "E313", {"start": v(-69.82, -34.08) * mm, "end": v(-70.66, -34) * mm});
            skLineSegment(sketch, "E314", {"start": v(-70.66, -34) * mm, "end": v(-71.16, -33.81) * mm});
            skLineSegment(sketch, "E315", {"start": v(-71.16, -33.81) * mm, "end": v(-71.96, -33.4) * mm});
            skLineSegment(sketch, "E316", {"start": v(-71.96, -33.4) * mm, "end": v(-72.37, -33.15) * mm});
            skLineSegment(sketch, "E317", {"start": v(-72.37, -33.15) * mm, "end": v(-73, -32.88) * mm});
            skLineSegment(sketch, "E318", {"start": v(-73, -32.88) * mm, "end": v(-73.4, -32.77) * mm});
            skLineSegment(sketch, "E319", {"start": v(-73.4, -32.77) * mm, "end": v(-74.73, -32.2) * mm});
            skLineSegment(sketch, "E320", {"start": v(-74.73, -32.2) * mm, "end": v(-75.8, -31.77) * mm});
            skLineSegment(sketch, "E321", {"start": v(-75.8, -31.77) * mm, "end": v(-77.15, -31.2) * mm});
            skLineSegment(sketch, "E322", {"start": v(-77.15, -31.2) * mm, "end": v(-78.26, -30.56) * mm});
            skLineSegment(sketch, "E323", {"start": v(-78.26, -30.56) * mm, "end": v(-79.23, -30.22) * mm});
            skLineSegment(sketch, "E324", {"start": v(-79.23, -30.22) * mm, "end": v(-80.22, -29.72) * mm});
            skLineSegment(sketch, "E325", {"start": v(-80.22, -29.72) * mm, "end": v(-80.49, -29.53) * mm});
            skLineSegment(sketch, "E326", {"start": v(-80.49, -29.53) * mm, "end": v(-80.54, -29.26) * mm});
            skLineSegment(sketch, "E327", {"start": v(-80.54, -29.26) * mm, "end": v(-80.18, -29.2) * mm});
            skLineSegment(sketch, "E328", {"start": v(-80.18, -29.2) * mm, "end": v(-78.9, -29.27) * mm});
            skLineSegment(sketch, "E329", {"start": v(-78.9, -29.27) * mm, "end": v(-77.89, -29.37) * mm});
            skLineSegment(sketch, "E330", {"start": v(-77.89, -29.37) * mm, "end": v(-77.26, -29.46) * mm});
            skLineSegment(sketch, "E331", {"start": v(-77.26, -29.46) * mm, "end": v(-77, -29.43) * mm});
            skLineSegment(sketch, "E332", {"start": v(-77, -29.43) * mm, "end": v(-76.95, -29.2) * mm});
            skLineSegment(sketch, "E333", {"start": v(-76.95, -29.2) * mm, "end": v(-77.78, -28.74) * mm});
            skLineSegment(sketch, "E334", {"start": v(-77.78, -28.74) * mm, "end": v(-79.06, -27.73) * mm});
            skLineSegment(sketch, "E335", {"start": v(-79.06, -27.73) * mm, "end": v(-79.78, -27.33) * mm});
            skLineSegment(sketch, "E336", {"start": v(-79.78, -27.33) * mm, "end": v(-81.1, -26.44) * mm});
            skLineSegment(sketch, "E337", {"start": v(-81.1, -26.44) * mm, "end": v(-81.61, -26.06) * mm});
            skLineSegment(sketch, "E338", {"start": v(-81.61, -26.06) * mm, "end": v(-81.54, -25.77) * mm});
            skLineSegment(sketch, "E339", {"start": v(-81.54, -25.77) * mm, "end": v(-81.35, -25.55) * mm});
            skLineSegment(sketch, "E340", {"start": v(-81.35, -25.55) * mm, "end": v(-80.77, -25) * mm});
            skLineSegment(sketch, "E341", {"start": v(-80.77, -25) * mm, "end": v(-80.21, -25.03) * mm});
            skLineSegment(sketch, "E342", {"start": v(-80.21, -25.03) * mm, "end": v(-79.17, -25.18) * mm});
            skLineSegment(sketch, "E343", {"start": v(-79.17, -25.18) * mm, "end": v(-77.96, -25.25) * mm});
            skLineSegment(sketch, "E344", {"start": v(-77.96, -25.25) * mm, "end": v(-76.4, -25.37) * mm});
            skLineSegment(sketch, "E345", {"start": v(-76.4, -25.37) * mm, "end": v(-75.44, -25.32) * mm});
            skLineSegment(sketch, "E346", {"start": v(-75.44, -25.32) * mm, "end": v(-74.39, -25.45) * mm});
            skLineSegment(sketch, "E347", {"start": v(-74.39, -25.45) * mm, "end": v(-74, -25.34) * mm});
            skLineSegment(sketch, "E348", {"start": v(-74, -25.34) * mm, "end": v(-74.04, -25.02) * mm});
            skLineSegment(sketch, "E349", {"start": v(-74.04, -25.02) * mm, "end": v(-74.77, -24.6) * mm});
            skLineSegment(sketch, "E350", {"start": v(-74.77, -24.6) * mm, "end": v(-75.76, -23.76) * mm});
            skLineSegment(sketch, "E351", {"start": v(-75.76, -23.76) * mm, "end": v(-76.91, -22.93) * mm});
            skLineSegment(sketch, "E352", {"start": v(-76.91, -22.93) * mm, "end": v(-78.3, -21.81) * mm});
            skLineSegment(sketch, "E353", {"start": v(-78.3, -21.81) * mm, "end": v(-78.46, -21.55) * mm});
            skLineSegment(sketch, "E354", {"start": v(-78.46, -21.55) * mm, "end": v(-77.97, -20.6) * mm});
            skLineSegment(sketch, "E355", {"start": v(-77.97, -20.6) * mm, "end": v(-76.54, -21.2) * mm});
            skLineSegment(sketch, "E356", {"start": v(-76.54, -21.2) * mm, "end": v(-75.31, -21.6) * mm});
            skLineSegment(sketch, "E357", {"start": v(-75.31, -21.6) * mm, "end": v(-73.77, -22.21) * mm});
            skLineSegment(sketch, "E358", {"start": v(-73.77, -22.21) * mm, "end": v(-71.18, -23.09) * mm});
            skLineSegment(sketch, "E359", {"start": v(-71.18, -23.09) * mm, "end": v(-69.02, -23.74) * mm});
            skLineSegment(sketch, "E360", {"start": v(-69.02, -23.74) * mm, "end": v(-67.15, -24.3) * mm});
            skLineSegment(sketch, "E361", {"start": v(-67.15, -24.3) * mm, "end": v(-64.44, -25.46) * mm});
            skLineSegment(sketch, "E362", {"start": v(-64.44, -25.46) * mm, "end": v(-62.7, -26.37) * mm});
            skLineSegment(sketch, "E363", {"start": v(-62.7, -26.37) * mm, "end": v(-60.9, -27.28) * mm});
            skLineSegment(sketch, "E364", {"start": v(-60.9, -27.28) * mm, "end": v(-59.51, -27.98) * mm});
            skLineSegment(sketch, "E365", {"start": v(-59.51, -27.98) * mm, "end": v(-59, -28.03) * mm});
            skLineSegment(sketch, "E366", {"start": v(-59, -28.03) * mm, "end": v(-57.97, -28.2) * mm});
            skLineSegment(sketch, "E367", {"start": v(-57.97, -28.2) * mm, "end": v(-56.85, -28.42) * mm});
            skLineSegment(sketch, "E368", {"start": v(-56.85, -28.42) * mm, "end": v(-55.1, -28.84) * mm});
            skLineSegment(sketch, "E369", {"start": v(-55.1, -28.84) * mm, "end": v(-54.25, -29.02) * mm});
            skLineSegment(sketch, "E370", {"start": v(-54.25, -29.02) * mm, "end": v(-52.02, -29.09) * mm});
            skLineSegment(sketch, "E371", {"start": v(-52.02, -29.09) * mm, "end": v(-50.46, -29.1) * mm});
            skLineSegment(sketch, "E372", {"start": v(-50.46, -29.1) * mm, "end": v(-49.72, -28.92) * mm});
            skLineSegment(sketch, "E373", {"start": v(-49.72, -28.92) * mm, "end": v(-49.23, -26.44) * mm});
            skLineSegment(sketch, "E374", {"start": v(-49.23, -26.44) * mm, "end": v(-49.04, -25.45) * mm});
            skLineSegment(sketch, "E375", {"start": v(-49.04, -25.45) * mm, "end": v(-48.44, -23.45) * mm});
            skLineSegment(sketch, "E376", {"start": v(-48.44, -23.45) * mm, "end": v(-47.85, -21.48) * mm});
            skLineSegment(sketch, "E377", {"start": v(-47.85, -21.48) * mm, "end": v(-47.3, -19.46) * mm});
            skLineSegment(sketch, "E378", {"start": v(-47.3, -19.46) * mm, "end": v(-46.71, -17.5) * mm});
            skLineSegment(sketch, "E379", {"start": v(-46.71, -17.5) * mm, "end": v(-46.46, -15.93) * mm});
            skLineSegment(sketch, "E380", {"start": v(-46.46, -15.93) * mm, "end": v(-46.8, -15.78) * mm});
            skLineSegment(sketch, "E381", {"start": v(-46.8, -15.78) * mm, "end": v(-48.05, -15.07) * mm});
            skLineSegment(sketch, "E382", {"start": v(-48.05, -15.07) * mm, "end": v(-48.92, -14.68) * mm});
            skLineSegment(sketch, "E383", {"start": v(-48.92, -14.68) * mm, "end": v(-49.8, -14.2) * mm});
            skLineSegment(sketch, "E384", {"start": v(-49.8, -14.2) * mm, "end": v(-54.4, -11.84) * mm});
            skLineSegment(sketch, "E385", {"start": v(-54.4, -11.84) * mm, "end": v(-57, -10.41) * mm});
            skLineSegment(sketch, "E386", {"start": v(-57, -10.41) * mm, "end": v(-58.48, -9.67) * mm});
            skLineSegment(sketch, "E387", {"start": v(-58.48, -9.67) * mm, "end": v(-59.06, -9.48) * mm});
            skLineSegment(sketch, "E388", {"start": v(-59.06, -9.48) * mm, "end": v(-59.54, -7.87) * mm});
            skLineSegment(sketch, "E389", {"start": v(-59.54, -7.87) * mm, "end": v(-59.65, -7.1) * mm});
            skLineSegment(sketch, "E390", {"start": v(-59.65, -7.1) * mm, "end": v(-59.9, -6.24) * mm});
            skLineSegment(sketch, "E391", {"start": v(-59.9, -6.24) * mm, "end": v(-56.9, -6.11) * mm});
            skLineSegment(sketch, "E392", {"start": v(-56.9, -6.11) * mm, "end": v(-56.65, -5.87) * mm});
            skLineSegment(sketch, "E393", {"start": v(-56.65, -5.87) * mm, "end": v(-56.62, -5.28) * mm});
            skLineSegment(sketch, "E394", {"start": v(-56.62, -5.28) * mm, "end": v(-56.58, -4.49) * mm});
            skLineSegment(sketch, "E395", {"start": v(-56.58, -4.49) * mm, "end": v(-56.78, -4.16) * mm});
            skLineSegment(sketch, "E396", {"start": v(-56.78, -4.16) * mm, "end": v(-57.99, -2.62) * mm});
            skLineSegment(sketch, "E397", {"start": v(-57.99, -2.62) * mm, "end": v(-57.4, -1.53) * mm});
            skLineSegment(sketch, "E398", {"start": v(-57.4, -1.53) * mm, "end": v(-57.03, -1.22) * mm});
            skLineSegment(sketch, "E399", {"start": v(-57.03, -1.22) * mm, "end": v(-55.87, -1.05) * mm});
            skLineSegment(sketch, "E400", {"start": v(-55.87, -1.05) * mm, "end": v(-55.12, -0.8) * mm});
            skLineSegment(sketch, "E401", {"start": v(-55.12, -0.8) * mm, "end": v(-55.01, 0.04) * mm});
            skLineSegment(sketch, "E402", {"start": v(-55.01, 0.04) * mm, "end": v(-54.86, 0.76) * mm});
            skLineSegment(sketch, "E403", {"start": v(-54.86, 0.76) * mm, "end": v(-53.42, 0.54) * mm});
            skLineSegment(sketch, "E404", {"start": v(-53.42, 0.54) * mm, "end": v(-52, 0.31) * mm});
            skLineSegment(sketch, "E405", {"start": v(-52, 0.31) * mm, "end": v(-51.06, 0.11) * mm});
            skLineSegment(sketch, "E406", {"start": v(-51.06, 0.11) * mm, "end": v(-50.09, -0.21) * mm});
            skLineSegment(sketch, "E407", {"start": v(-50.09, -0.21) * mm, "end": v(-49.67, -0.68) * mm});
            skLineSegment(sketch, "E408", {"start": v(-49.67, -0.68) * mm, "end": v(-49.39, -1.24) * mm});
            skLineSegment(sketch, "E409", {"start": v(-49.39, -1.24) * mm, "end": v(-48.93, -1.84) * mm});
            skLineSegment(sketch, "E410", {"start": v(-48.93, -1.84) * mm, "end": v(-48.58, -2.83) * mm});
            skLineSegment(sketch, "E411", {"start": v(-48.58, -2.83) * mm, "end": v(-48.73, -3.1) * mm});
            skLineSegment(sketch, "E412", {"start": v(-48.73, -3.1) * mm, "end": v(-49.62, -3.1) * mm});
            skLineSegment(sketch, "E413", {"start": v(-49.62, -3.1) * mm, "end": v(-50.83, -2.9) * mm});
            skLineSegment(sketch, "E414", {"start": v(-50.83, -2.9) * mm, "end": v(-51.15, -2.9) * mm});
            skLineSegment(sketch, "E415", {"start": v(-51.15, -2.9) * mm, "end": v(-50.76, -3.29) * mm});
            skLineSegment(sketch, "E416", {"start": v(-50.76, -3.29) * mm, "end": v(-50.26, -3.56) * mm});
            skLineSegment(sketch, "E417", {"start": v(-50.26, -3.56) * mm, "end": v(-49.2, -4.53) * mm});
            skLineSegment(sketch, "E418", {"start": v(-49.2, -4.53) * mm, "end": v(-49.24, -4.98) * mm});
            skLineSegment(sketch, "E419", {"start": v(-49.24, -4.98) * mm, "end": v(-49.45, -5.06) * mm});
            skLineSegment(sketch, "E420", {"start": v(-49.45, -5.06) * mm, "end": v(-49.45, -5.22) * mm});
            skLineSegment(sketch, "E421", {"start": v(-49.45, -5.22) * mm, "end": v(-49.53, -5.54) * mm});
            skLineSegment(sketch, "E422", {"start": v(-49.53, -5.54) * mm, "end": v(-49.51, -5.76) * mm});
            skLineSegment(sketch, "E423", {"start": v(-49.51, -5.76) * mm, "end": v(-49.66, -5.9) * mm});
            skLineSegment(sketch, "E424", {"start": v(-49.66, -5.9) * mm, "end": v(-49.84, -6.06) * mm});
            skLineSegment(sketch, "E425", {"start": v(-49.84, -6.06) * mm, "end": v(-50.07, -6.18) * mm});
            skLineSegment(sketch, "E426", {"start": v(-50.07, -6.18) * mm, "end": v(-51.44, -6.17) * mm});
            skLineSegment(sketch, "E427", {"start": v(-51.44, -6.17) * mm, "end": v(-52.69, -5.85) * mm});
            skLineSegment(sketch, "E428", {"start": v(-52.69, -5.85) * mm, "end": v(-53.42, -5.71) * mm});
            skLineSegment(sketch, "E429", {"start": v(-53.42, -5.71) * mm, "end": v(-53.71, -5.76) * mm});
            skLineSegment(sketch, "E430", {"start": v(-53.71, -5.76) * mm, "end": v(-53.68, -5.95) * mm});
            skLineSegment(sketch, "E431", {"start": v(-53.68, -5.95) * mm, "end": v(-53.23, -6.27) * mm});
            skLineSegment(sketch, "E432", {"start": v(-53.23, -6.27) * mm, "end": v(-51.92, -6.87) * mm});
            skLineSegment(sketch, "E433", {"start": v(-51.92, -6.87) * mm, "end": v(-51.26, -7.23) * mm});
            skLineSegment(sketch, "E434", {"start": v(-51.26, -7.23) * mm, "end": v(-50.69, -7.48) * mm});
            skLineSegment(sketch, "E435", {"start": v(-50.69, -7.48) * mm, "end": v(-50.42, -7.75) * mm});
            skLineSegment(sketch, "E436", {"start": v(-50.42, -7.75) * mm, "end": v(-50.45, -8) * mm});
            skLineSegment(sketch, "E437", {"start": v(-50.45, -8) * mm, "end": v(-50.76, -8.24) * mm});
            skLineSegment(sketch, "E438", {"start": v(-50.76, -8.24) * mm, "end": v(-51.36, -8.84) * mm});
            skLineSegment(sketch, "E439", {"start": v(-51.36, -8.84) * mm, "end": v(-51.62, -9.01) * mm});
            skLineSegment(sketch, "E440", {"start": v(-51.62, -9.01) * mm, "end": v(-51.24, -9.13) * mm});
            skLineSegment(sketch, "E441", {"start": v(-51.24, -9.13) * mm, "end": v(-49.9, -9) * mm});
            skLineSegment(sketch, "E442", {"start": v(-49.9, -9) * mm, "end": v(-48.62, -9) * mm});
            skLineSegment(sketch, "E443", {"start": v(-48.62, -9) * mm, "end": v(-46.94, -9.06) * mm});
            skLineSegment(sketch, "E444", {"start": v(-46.94, -9.06) * mm, "end": v(-45.84, -9.26) * mm});
            skLineSegment(sketch, "E445", {"start": v(-45.84, -9.26) * mm, "end": v(-44.12, -9.6) * mm});
            skLineSegment(sketch, "E446", {"start": v(-44.12, -9.6) * mm, "end": v(-43.37, -9.98) * mm});
            skLineSegment(sketch, "E447", {"start": v(-43.37, -9.98) * mm, "end": v(-42.75, -10.12) * mm});
            skLineSegment(sketch, "E448", {"start": v(-42.75, -10.12) * mm, "end": v(-41.98, -10.52) * mm});
            skLineSegment(sketch, "E449", {"start": v(-41.98, -10.52) * mm, "end": v(-40.78, -10.77) * mm});
            skLineSegment(sketch, "E450", {"start": v(-40.78, -10.77) * mm, "end": v(-40.47, -10.8) * mm});
            skLineSegment(sketch, "E451", {"start": v(-40.47, -10.8) * mm, "end": v(-39.86, -10.35) * mm});
            skLineSegment(sketch, "E452", {"start": v(-39.86, -10.35) * mm, "end": v(-39.29, -9.84) * mm});
            skLineSegment(sketch, "E453", {"start": v(-39.29, -9.84) * mm, "end": v(-39.01, -9.48) * mm});
            skLineSegment(sketch, "E454", {"start": v(-39.01, -9.48) * mm, "end": v(-38.56, -8.97) * mm});
            skLineSegment(sketch, "E455", {"start": v(-38.56, -8.97) * mm, "end": v(-38.33, -8.57) * mm});
            skLineSegment(sketch, "E456", {"start": v(-38.33, -8.57) * mm, "end": v(-37.86, -7.65) * mm});
            skLineSegment(sketch, "E457", {"start": v(-37.86, -7.65) * mm, "end": v(-37.52, -7.23) * mm});
            skLineSegment(sketch, "E458", {"start": v(-37.52, -7.23) * mm, "end": v(-37.28, -6.6) * mm});
            skLineSegment(sketch, "E459", {"start": v(-37.28, -6.6) * mm, "end": v(-37.1, -6.11) * mm});
            skLineSegment(sketch, "E460", {"start": v(-37.1, -6.11) * mm, "end": v(-37.06, -5.69) * mm});
            skLineSegment(sketch, "E461", {"start": v(-37.06, -5.69) * mm, "end": v(-37.24, -4.69) * mm});
            skLineSegment(sketch, "E462", {"start": v(-37.24, -4.69) * mm, "end": v(-37.39, -4.3) * mm});
            skLineSegment(sketch, "E463", {"start": v(-37.39, -4.3) * mm, "end": v(-37.62, -3.7) * mm});
            skLineSegment(sketch, "E464", {"start": v(-37.62, -3.7) * mm, "end": v(-37.9, -3.47) * mm});
            skLineSegment(sketch, "E465", {"start": v(-37.9, -3.47) * mm, "end": v(-38.44, -3.26) * mm});
            skLineSegment(sketch, "E466", {"start": v(-38.44, -3.26) * mm, "end": v(-39.9, -2.72) * mm});
            skLineSegment(sketch, "E467", {"start": v(-39.9, -2.72) * mm, "end": v(-40.48, -2.56) * mm});
            skLineSegment(sketch, "E468", {"start": v(-40.48, -2.56) * mm, "end": v(-41.19, -2.33) * mm});
            skLineSegment(sketch, "E469", {"start": v(-41.19, -2.33) * mm, "end": v(-41.78, -2.16) * mm});
            skLineSegment(sketch, "E470", {"start": v(-41.78, -2.16) * mm, "end": v(-43, -1.57) * mm});
            skLineSegment(sketch, "E471", {"start": v(-43, -1.57) * mm, "end": v(-43.85, -1.3) * mm});
            skLineSegment(sketch, "E472", {"start": v(-43.85, -1.3) * mm, "end": v(-44.38, -1.1) * mm});
            skLineSegment(sketch, "E473", {"start": v(-44.38, -1.1) * mm, "end": v(-45.03, -0.98) * mm});
            skLineSegment(sketch, "E474", {"start": v(-45.03, -0.98) * mm, "end": v(-45.59, -0.82) * mm});
            skLineSegment(sketch, "E475", {"start": v(-45.59, -0.82) * mm, "end": v(-45.68, -0.48) * mm});
            skLineSegment(sketch, "E476", {"start": v(-45.68, -0.48) * mm, "end": v(-44.76, -0.2) * mm});
            skLineSegment(sketch, "E477", {"start": v(-44.76, -0.2) * mm, "end": v(-44.28, -0.12) * mm});
            skLineSegment(sketch, "E478", {"start": v(-44.28, -0.12) * mm, "end": v(-44.09, -0.05) * mm});
            skLineSegment(sketch, "E479", {"start": v(-44.09, -0.05) * mm, "end": v(-44, 0.22) * mm});
            skLineSegment(sketch, "E480", {"start": v(-44, 0.22) * mm, "end": v(-44.02, 0.46) * mm});
            skLineSegment(sketch, "E481", {"start": v(-44.02, 0.46) * mm, "end": v(-44.03, 0.67) * mm});
            skLineSegment(sketch, "E482", {"start": v(-44.03, 0.67) * mm, "end": v(-44.08, 0.88) * mm});
            skLineSegment(sketch, "E483", {"start": v(-44.08, 0.88) * mm, "end": v(-44.73, 0.94) * mm});
            skLineSegment(sketch, "E484", {"start": v(-44.73, 0.94) * mm, "end": v(-45.63, 1.02) * mm});
            skLineSegment(sketch, "E485", {"start": v(-45.63, 1.02) * mm, "end": v(-46.15, 1.14) * mm});
            skLineSegment(sketch, "E486", {"start": v(-46.15, 1.14) * mm, "end": v(-46.75, 1.26) * mm});
            skLineSegment(sketch, "E487", {"start": v(-46.75, 1.26) * mm, "end": v(-47.04, 1.46) * mm});
            skLineSegment(sketch, "E488", {"start": v(-47.04, 1.46) * mm, "end": v(-47.32, 1.65) * mm});
            skLineSegment(sketch, "E489", {"start": v(-47.32, 1.65) * mm, "end": v(-47.53, 1.92) * mm});
            skLineSegment(sketch, "E490", {"start": v(-47.53, 1.92) * mm, "end": v(-47.58, 2.25) * mm});
            skLineSegment(sketch, "E491", {"start": v(-47.58, 2.25) * mm, "end": v(-47.65, 2.47) * mm});
            skLineSegment(sketch, "E492", {"start": v(-47.65, 2.47) * mm, "end": v(-47.5, 2.74) * mm});
            skSolve(sketch);
        }
        {
            var Q0;
            Q0 = qSketchRegion(id + "F2", true);
            extrude(context, id + "F3", {"entities" : qUnion([Q0]), "operationType" : NewBodyOperationType.REMOVE, "depth" : 30 * mm, "offsetDistance" : 25 * mm});
        }
        {
            var Q0;
            Q0=makeQuery(id+"F1.opExtrude","CAP_FACE",FACE,{"disambiguationData":[OSD([sQuery(id+"F0.wireOp",EDGE,"E0"),sQuery(id+"F0.wireOp",EDGE,"E1"),sQuery(id+"F0.wireOp",EDGE,"E2")])],"isStart":false});
            var sketch = newSketch(context, id + "F4", { "sketchPlane" : qUnion([Q0])});
            skCircle(sketch, "E493", {"center": v(-2.52, 30.93) * mm, "radius": 1.96 * mm});
            skSolve(sketch);
        }
        {
            var Q0;
            Q0 = qSketchRegion(id + "F4", true);
            extrude(context, id + "F5", {"entities" : qUnion([Q0]), "operationType" : NewBodyOperationType.REMOVE, "oppositeDirection" : true, "depth" : 60 * mm, "offsetDistance" : 25 * mm});
        }
    });
